# Revit family: Stair_Tread-Wooster-Supergrit_Safety_Treads-121_121BF
name_source: partatom
category: Specialty Equipment
revit_build: Autodesk Revit 2017 (Build: 20160720_1515(x64)
units: mm (PartAtom-declared; Revit-internal decimal feet)

## family parameters
Cut with Voids When Loaded = No
Host = Face
OmniClass Number = 23.30.70.21.11.11.11
OmniClass Title = Stair Nosings
Part Type = Normal
Room Calculation Point = No
Round Connector Dimension = Use Diameter
Shared = No

## types (2) — shared parameters
Default Elevation = 0' - 0"
Depth = 0' - 0 1/4"
Description = Anti-Slip Stair Nosing
Manufacturer = Wooster Productions Inc
Manufacturer Fax Number = 330-262-4151
Product Documentation Link = http://www.woosterproducts.com
Product Name = Supergrit Nosings / Warning Strips
Product Page URL = http://www.woosterproducts.com
URL = http://www.wooster-products.com
Version = 2017 - v2.0a

## per-type parameters (varying)
| type | Existing Construction | New Construction |
| 121BF | No | Yes |
| 121 | Yes | No |

note: column(s) folded — value = type name in every type: Model

## geometry (parser evidence)
native form markers: Blend x14, Sweep x4
no freeform markers — native parametric forms only
